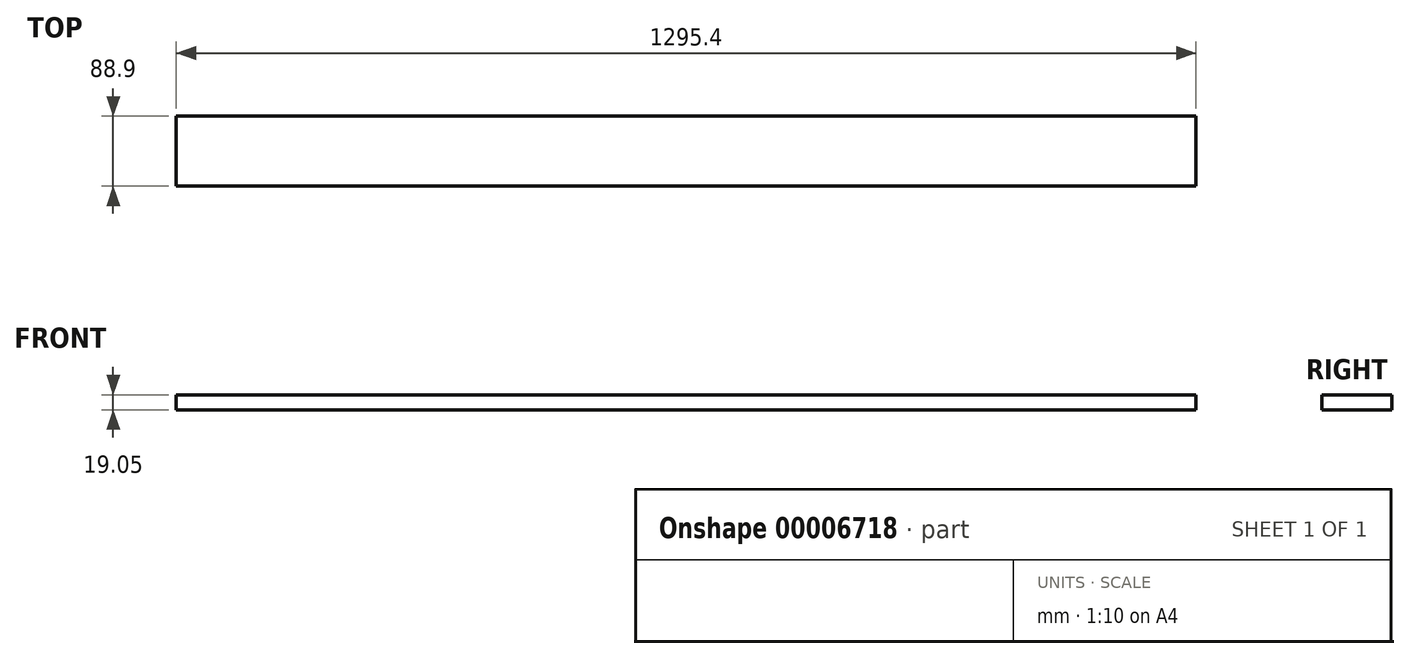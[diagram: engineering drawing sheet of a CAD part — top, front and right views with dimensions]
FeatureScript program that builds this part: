
annotation { "Feature Type Name" : "Feature", "Feature Type Description" : "" }
export const myFeature = defineFeature(function(context is Context, id is Id, definition is map)
    precondition{}
    {
        {
            var Q0;
            Q0=qCreatedBy(makeId("Top.planeOp"),FACE);
            var sketch = newSketch(context, id + "F0", { "sketchPlane" : qUnion([Q0])});
            skLineSegment(sketch, "E0.bottom", {"start": v(-647.7, 44.45) * mm, "end": v(647.7, 44.45) * mm});
            skLineSegment(sketch, "E0.top", {"start": v(-647.7, -44.45) * mm, "end": v(647.7, -44.45) * mm});
            skLineSegment(sketch, "E0.left", {"start": v(-647.7, 44.45) * mm, "end": v(-647.7, -44.45) * mm});
            skLineSegment(sketch, "E0.right", {"start": v(647.7, 44.45) * mm, "end": v(647.7, -44.45) * mm});
            skSolve(sketch);
        }
        {
            var Q0;
            Q0=makeQuery(id+"F0.imprint","IMPRINT",FACE,{"disambiguationData":[TD([[makeQuery(id+"F0.imprint","IMPRINT",EDGE,{"derivedFrom":sQuery(id+"F0.wireOp",EDGE,"E0.bottom")}),-1.0]])]});
            extrude(context, id + "F1", {"entities" : qUnion([Q0]), "depth" : 19.05 * mm});
        }
    });
